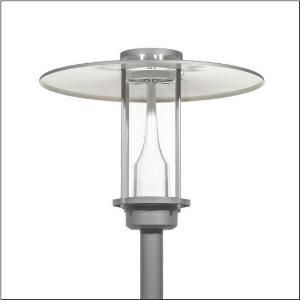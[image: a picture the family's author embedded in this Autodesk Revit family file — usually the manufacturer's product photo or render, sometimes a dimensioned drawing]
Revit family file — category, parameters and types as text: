
# Revit family: city-light_plus_iq___p1_0a_5xa5275ff14hp_3a67
name_source: partatom
category: Lighting Fixtures
units: mm (PartAtom-declared; Revit-internal decimal feet)

## family parameters
Cut with Voids When Loaded = No
Host = Face
Light Source = No
Part Type = Normal
Room Calculation Point = No
Round Connector Dimension = Use Diameter
Shared = No

## types (1)
- --- (1 x LED, 4480 lm, 33.6 W, 3000K)
    Apparent Load = 34 VA
    CIE Flux Codes = 30 60 90 96 100
    Color Rendering = 70
    Color Temperature = 3000K
    Default Elevation = 1800 mm
    Description = City-Light Plus iQ, mast luminaire, Module 540 iQ-SR, primary light control with 3 zone facetted reflector, of plastic, silver coated, highly specular, structured, primary optical cover: cover, of PMMA, transparent, light distribution: P1.0a, light emission: direct distribution, primary light characteristic: strongly asymmetric, installation type: post-top, LED, High Power LED, rated luminous flux: 4.480lm, luminous efficacy: 133lm/W, light colour: 730, colour temperature: 3000K, control gear: ECG iQ, control: pre-setting: logarithmic dimming characteristic, Street-Remote, Auto-Match, Temp-Guard, Lumen-Switch, Night-Set, Smart-Wire, Light-Fading, Desk-Remote (wireless, voltage-free reading and setting of iQ features in the workshop via application-optimized NFC function/RFID function), optimised constant luminous flux control (CLO 2.0), with terminal, 6-pole, max. 2.5mm², mains connection: 230..240V, AC, 50/60Hz, start of lifetime: 34W, end of service life: 36W, reduction: 15W, luminaire housing, upper part, of glass-fibre reinforced polyester, coated, Siteco® metallic grey (DB 702S), diameter: 750mm, height: 590mm, spigot size: d x l = 76 x 70mm (post-top) | with reducer (optional accessory) 60 x 70mm, post-top mast mounting element, of diecast aluminium, coated, Siteco® metallic grey (DB 702S), Module 540 iQ-SR, traffic white (RAL 9016), equipment: Power, protection rating (complete): IP65, insulation class (complete): insulation class II (safety insulation), certification: CE, ENEC, VDE, packaging unit: 1 piece

Light Distribution: P1.0a
    Height = 590 mm
    Lamp = 1 x LED
    Lamp Light Flux = 4480 lm
    Lamp Power = 33.6 W
    Lamp count = 1
    Length = 750 mm
    Luminous efficacy = 133 lm/W
    Manufacturer = Siteco
    ModVariant = No
    Model = 5XA5275FF14HP
    Number of Poles = 1
    OnlyDefault = Yes
    Power Factor = 1
    Product Name = City-Light Plus iQ | P1.0a
    Product group = mast luminaire | pylon top
    ProductGroupID = 6100
    Protection Class = Protection class II
    Protection Degree = IP 65
    RLX_Detail_Level = 1
    RLX_Emergency_Light_Flux = 0 lm
    RLX_Emergency_Type = 0
    RLX_Emergency_Type_DB = No
    RlxData = <blob elided: 52617 chars, md5=af19b71c>
    Socket = socket
    Standby Power = 0 W
    System Light Flux = 4480 lm
    System Power = 34 W
    Type Comments = factory setting: luminous flux: 100 % | dim-lin: 254 | 695 mA
    Type Image = l_1006456.jpg
    URL = http://relux.com
    VarID = @adj_166419
    Voltage = 0 V
    Weight = 0.00 kg
    Width = 0 mm  [stored 0 ft]

note: [stored X ft] marks values corroborated as IEEE doubles in the binary element streams (Revit-internal decimal feet)

## geometry (parser evidence)
native form markers: Blend x4, Sweep x9
no freeform markers — native parametric forms only
